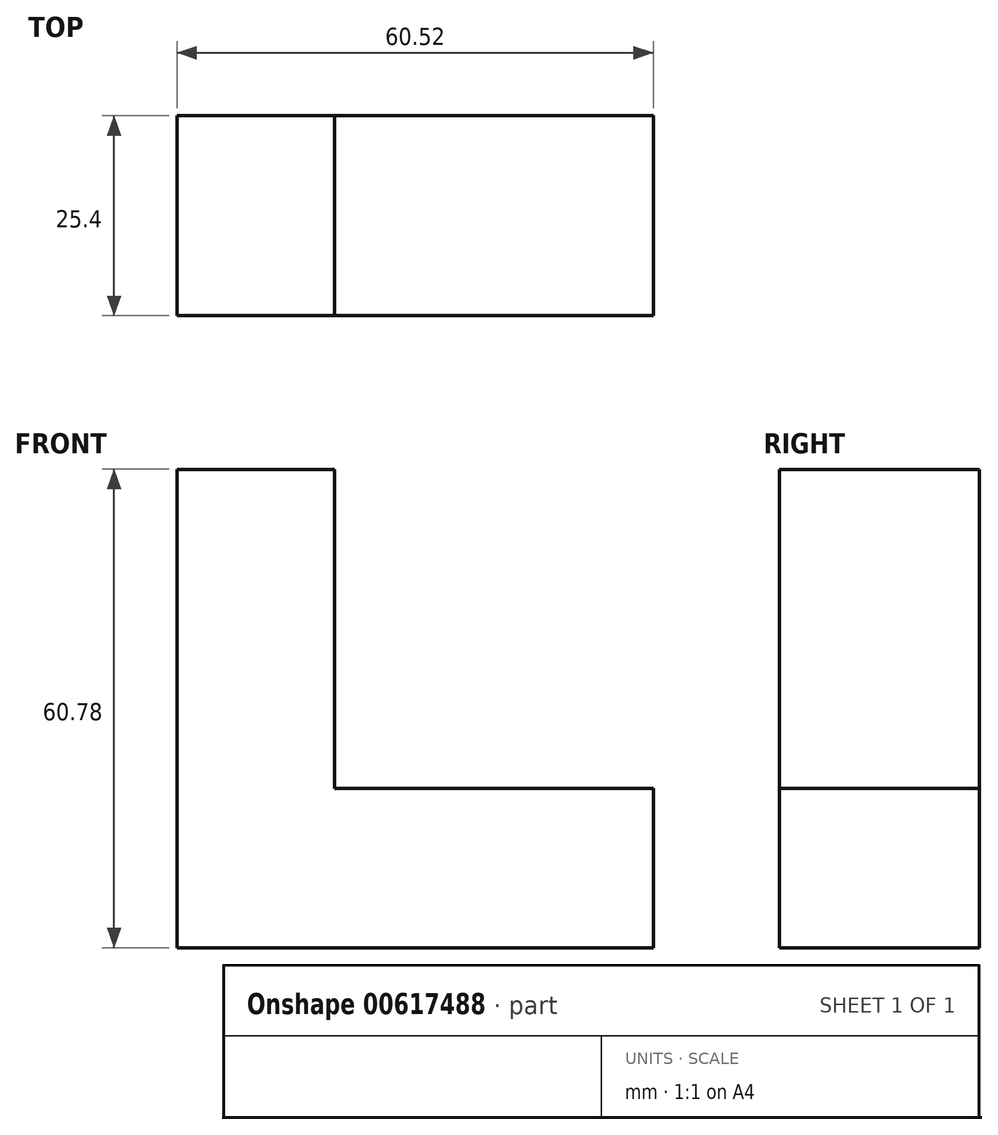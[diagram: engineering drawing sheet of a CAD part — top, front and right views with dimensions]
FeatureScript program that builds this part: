
annotation { "Feature Type Name" : "Feature", "Feature Type Description" : "" }
export const myFeature = defineFeature(function(context is Context, id is Id, definition is map)
    precondition{}
    {
        {
            var Q0;
            Q0=qCreatedBy(makeId("Front.planeOp"),FACE);
            var sketch = newSketch(context, id + "F0", { "sketchPlane" : qUnion([Q0])});
            skLineSegment(sketch, "E0", {"start": v(0, 0) * mm, "end": v(0, 20.26) * mm});
            skLineSegment(sketch, "E1", {"start": v(0, 20.26) * mm, "end": v(0, 40.52) * mm});
            skLineSegment(sketch, "E2", {"start": v(0, 40.52) * mm, "end": v(0, 60.78) * mm});
            skLineSegment(sketch, "E3", {"start": v(0, 60.78) * mm, "end": v(20, 60.78) * mm});
            skLineSegment(sketch, "E4", {"start": v(20, 60.78) * mm, "end": v(20, 40.52) * mm});
            skLineSegment(sketch, "E5", {"start": v(20, 40.52) * mm, "end": v(20, 20.26) * mm});
            skLineSegment(sketch, "E6", {"start": v(20, 20.26) * mm, "end": v(20, 0) * mm});
            skLineSegment(sketch, "E7", {"start": v(20, 0) * mm, "end": v(0, 0) * mm});
            skLineSegment(sketch, "E8", {"start": v(0, 20.26) * mm, "end": v(20, 20.26) * mm});
            skLineSegment(sketch, "E9", {"start": v(20, 40.52) * mm, "end": v(0, 40.52) * mm});
            skLineSegment(sketch, "E10", {"start": v(20, 0) * mm, "end": v(40, 0) * mm});
            skLineSegment(sketch, "E11", {"start": v(40, 0) * mm, "end": v(60.52, 0) * mm});
            skLineSegment(sketch, "E12", {"start": v(60.52, 0) * mm, "end": v(60.52, 20.26) * mm});
            skLineSegment(sketch, "E13", {"start": v(60.52, 20.26) * mm, "end": v(40, 20.26) * mm});
            skLineSegment(sketch, "E14", {"start": v(40, 20.26) * mm, "end": v(20, 20.26) * mm});
            skLineSegment(sketch, "E15", {"start": v(40, 20.26) * mm, "end": v(40, 0) * mm});
            skSolve(sketch);
        }
        {
            var Q0;
            Q0 = qSketchRegion(id + "F0", true);
            extrude(context, id + "F1", {"entities" : qUnion([Q0]), "depth" : 25.4 * mm, "offsetDistance" : 25.4 * mm});
        }
    });
